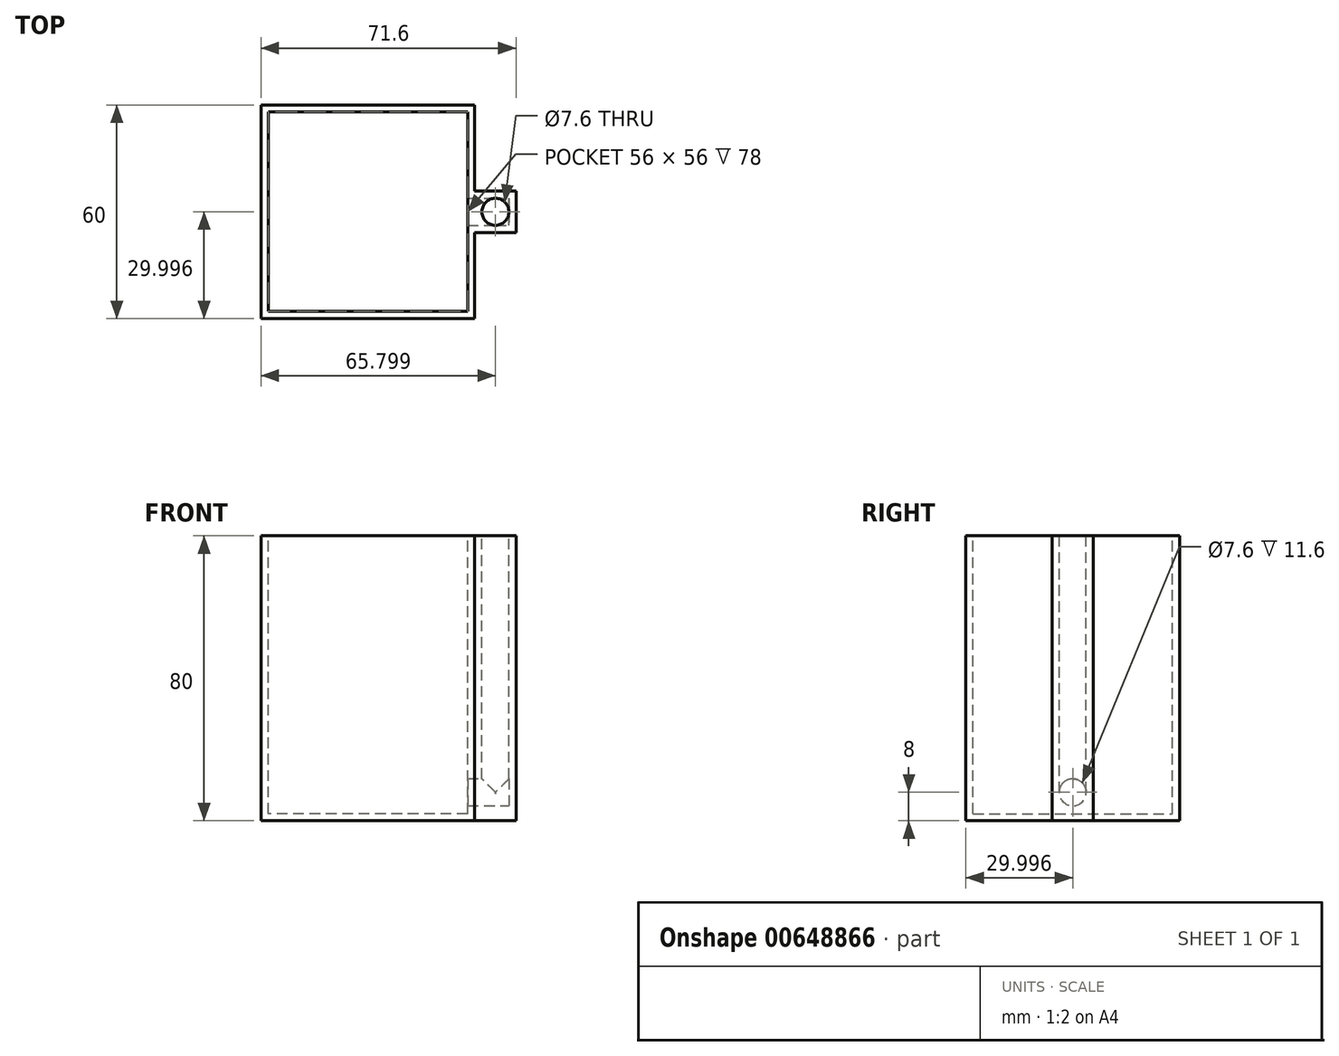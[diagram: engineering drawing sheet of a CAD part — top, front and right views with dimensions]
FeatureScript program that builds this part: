
annotation { "Feature Type Name" : "Feature", "Feature Type Description" : "" }
export const myFeature = defineFeature(function(context is Context, id is Id, definition is map)
    precondition{}
    {
        {
            var Q0;
            Q0=qCreatedBy(makeId("Top.planeOp"),FACE);
            var sketch = newSketch(context, id + "F0", { "sketchPlane" : qUnion([Q0])});
            skLineSegment(sketch, "E0.bottom", {"start": v(-10.74, 46.45) * mm, "end": v(49.26, 46.45) * mm});
            skLineSegment(sketch, "E0.top", {"start": v(-10.74, -13.55) * mm, "end": v(49.26, -13.55) * mm});
            skLineSegment(sketch, "E0.left", {"start": v(-10.74, 46.45) * mm, "end": v(-10.74, -13.55) * mm});
            skLineSegment(sketch, "E0.right", {"start": v(49.26, 46.45) * mm, "end": v(49.26, -13.55) * mm});
            skSolve(sketch);
        }
        {
            var Q0;
            Q0=makeQuery(id+"F0.imprint","IMPRINT",FACE,{"disambiguationData":[TD([[makeQuery(id+"F0.imprint","IMPRINT",EDGE,{"derivedFrom":sQuery(id+"F0.wireOp",EDGE,"E0.bottom")}),-1.0]])]});
            extrude(context, id + "F1", {"entities" : qUnion([Q0]), "depth" : 80 * mm, "offsetDistance" : 25 * mm});
        }
        {
            var Q0;
            Q0=makeQuery(id+"F1.opExtrude","CAP_FACE",FACE,{"disambiguationData":[OSD([sQuery(id+"F0.wireOp",EDGE,"E0.bottom"),sQuery(id+"F0.wireOp",EDGE,"E0.top"),sQuery(id+"F0.wireOp",EDGE,"E0.left"),sQuery(id+"F0.wireOp",EDGE,"E0.right")])],"isStart":false});
            var sketch = newSketch(context, id + "F2", { "sketchPlane" : qUnion([Q0])});
            skLineSegment(sketch, "E1.0", {"start": v(-8.74, 44.45) * mm, "end": v(47.26, 44.45) * mm});
            skLineSegment(sketch, "E1.1", {"start": v(-8.74, 44.45) * mm, "end": v(-8.74, -11.55) * mm});
            skLineSegment(sketch, "E1.2", {"start": v(-8.74, -11.55) * mm, "end": v(47.26, -11.55) * mm});
            skLineSegment(sketch, "E1.3", {"start": v(47.26, 44.45) * mm, "end": v(47.26, -11.55) * mm});
            skSolve(sketch);
        }
        {
            var Q0;
            Q0=makeQuery(id+"F2.imprint","IMPRINT",FACE,{"disambiguationData":[TD([[makeQuery(id+"F2.imprint","IMPRINT",EDGE,{"derivedFrom":sQuery(id+"F2.wireOp",EDGE,"E1.0")}),-1.0]])]});
            var Q1;
            Q1=makeQuery(id+"F1.opExtrude","CAP_FACE",FACE,{"disambiguationData":[OSD([sQuery(id+"F0.wireOp",EDGE,"E0.bottom"),sQuery(id+"F0.wireOp",EDGE,"E0.top"),sQuery(id+"F0.wireOp",EDGE,"E0.left"),sQuery(id+"F0.wireOp",EDGE,"E0.right")])],"isStart":true});
            extrude(context, id + "F3", {"entities" : qUnion([Q0]), "operationType" : NewBodyOperationType.REMOVE, "endBound" : BoundingType.UP_TO_SURFACE, "oppositeDirection" : true, "depth" : 25 * mm, "endBoundEntityFace" : qUnion([Q1]), "hasOffset" : true, "offsetDistance" : 2 * mm});
        }
        {
            var Q0;
            Q0=makeQuery(id+"F1.opExtrude","SWEPT_FACE",FACE,{"disambiguationData":[OSD([sQuery(id+"F0.wireOp",EDGE,"E0.right")])]});
            var sketch = newSketch(context, id + "F4", { "sketchPlane" : qUnion([Q0])});
            skCircle(sketch, "E2", {"center": v(16.45, 8) * mm, "radius": 3.8 * mm});
            skSolve(sketch);
        }
        {
            var Q0;
            Q0=makeQuery(id+"F4.imprint","IMPRINT",FACE,{"disambiguationData":[TD([[makeQuery(id+"F4.imprint","IMPRINT",EDGE,{"derivedFrom":sQuery(id+"F4.wireOp",EDGE,"E2")}),-1.0]])]});
            var sketch = newSketch(context, id + "F5", { "sketchPlane" : qUnion([Q0])});
            skLineSegment(sketch, "E3.bottom", {"start": v(10.65, 80) * mm, "end": v(22.25, 80) * mm});
            skLineSegment(sketch, "E3.top", {"start": v(10.65, 0) * mm, "end": v(22.25, 0) * mm});
            skLineSegment(sketch, "E3.left", {"start": v(10.65, 80) * mm, "end": v(10.65, 0) * mm});
            skLineSegment(sketch, "E3.right", {"start": v(22.25, 80) * mm, "end": v(22.25, 0) * mm});
            skSolve(sketch);
        }
        {
            var Q0;
            Q0=makeQuery(id+"F5.imprint","IMPRINT",FACE,{"disambiguationData":[TD([[makeQuery(id+"F5.imprint","IMPRINT",EDGE,{"derivedFrom":makeQuery(id+"F4.imprint","IMPRINT",EDGE,{"derivedFrom":sQuery(id+"F4.wireOp",EDGE,"E2")})}),1.0]])]});
            extrude(context, id + "F6", {"entities" : qUnion([Q0]), "operationType" : NewBodyOperationType.REMOVE, "oppositeDirection" : true, "depth" : 25 * mm, "offsetDistance" : 25 * mm});
        }
        {
            var Q0;
            Q0 = qSketchRegion(id + "F5", true);
            extrude(context, id + "F7", {"entities" : qUnion([Q0]), "operationType" : NewBodyOperationType.ADD, "depth" : (7.6 + 4) * mm, "offsetDistance" : 25 * mm});
        }
        {
            var Q0;
            Q0=makeQuery(id+"F7.boolean.opBoolean","MERGE",FACE,{"derivedFrom":[makeQuery(id+"F1.opExtrude","CAP_FACE",FACE,{"disambiguationData":[OSD([sQuery(id+"F0.wireOp",EDGE,"E0.bottom"),sQuery(id+"F0.wireOp",EDGE,"E0.top"),sQuery(id+"F0.wireOp",EDGE,"E0.left"),sQuery(id+"F0.wireOp",EDGE,"E0.right")])],"isStart":false}),makeQuery(id+"F7.opExtrude","SWEPT_FACE",FACE,{"disambiguationData":[OSD([sQuery(id+"F5.wireOp",EDGE,"E3.bottom")])]})]});
            var sketch = newSketch(context, id + "F8", { "sketchPlane" : qUnion([Q0])});
            skCircle(sketch, "E4", {"center": v(55.06, 16.45) * mm, "radius": 3.8 * mm});
            skPoint(sketch, "E4.centerSnap0", {"position": v(60.86, 16.45) * mm});
            skPoint(sketch, "E4.centerSnap1", {"position": v(55.06, 22.25) * mm});
            skSolve(sketch);
        }
        {
            var Q0;
            Q0=makeQuery(id+"F8.imprint","IMPRINT",FACE,{"disambiguationData":[TD([[makeQuery(id+"F8.imprint","IMPRINT",EDGE,{"derivedFrom":sQuery(id+"F8.wireOp",EDGE,"E4")}),1.0]])]});
            var Q1;
            Q1=makeQuery(id+"F7.boolean.opBoolean","MERGE",FACE,{"derivedFrom":[makeQuery(id+"F1.opExtrude","CAP_FACE",FACE,{"disambiguationData":[OSD([sQuery(id+"F0.wireOp",EDGE,"E0.bottom"),sQuery(id+"F0.wireOp",EDGE,"E0.top"),sQuery(id+"F0.wireOp",EDGE,"E0.left"),sQuery(id+"F0.wireOp",EDGE,"E0.right")])],"isStart":true}),makeQuery(id+"F7.opExtrude","SWEPT_FACE",FACE,{"disambiguationData":[OSD([sQuery(id+"F5.wireOp",EDGE,"E3.top")])]})]});
            extrude(context, id + "F9", {"entities" : qUnion([Q0]), "operationType" : NewBodyOperationType.REMOVE, "endBound" : BoundingType.UP_TO_SURFACE, "oppositeDirection" : true, "depth" : 74.7 * mm, "endBoundEntityFace" : qUnion([Q1]), "hasOffset" : true, "offsetDistance" : (4.2 + 3.6) * mm});
        }
        {
            var Q0;
            Q0 = qSketchRegion(id + "F4", true);
            var Q1;
            Q1=makeQuery(id+"F7.opExtrude","CAP_FACE",FACE,{"disambiguationData":[OSD([sQuery(id+"F5.wireOp",EDGE,"E3.bottom"),sQuery(id+"F5.wireOp",EDGE,"E3.top"),sQuery(id+"F5.wireOp",EDGE,"E3.left"),sQuery(id+"F5.wireOp",EDGE,"E3.right")])],"isStart":false});
            extrude(context, id + "F10", {"entities" : qUnion([Q0]), "operationType" : NewBodyOperationType.REMOVE, "endBound" : BoundingType.UP_TO_SURFACE, "depth" : 5.3 * mm, "endBoundEntityFace" : qUnion([Q1]), "hasOffset" : true, "offsetDistance" : 2 * mm});
        }
    });
